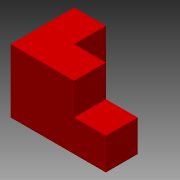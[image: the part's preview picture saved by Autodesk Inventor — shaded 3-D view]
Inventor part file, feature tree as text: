
AUTODESK INVENTOR PART (.ipt)
format: ipt  version: 2013 (Build 170138000, 138)  size: 99,840 bytes
history: native  units: in
note: dims shown in document units (in); Inventor stores cm internally (conversion verified against a paired STEP export)
features: extrude x3, sketch x3
ambient origin geometry x8: Origin, YZ Plane, XZ Plane, XY Plane, X Axis, Y Axis, Z Axis, Center Point
bodies: Solid1 (feature_tree)
feature tree (6):
  extrude  "Extrusion1"  Depth=0.75in
  extrude  "Extrusion2"  Depth=1.5in
  extrude  "Extrusion3"  Depth=0.75in TaperAngle=0.0deg
  sketch  "Sketch1"  dims[d0=2.25in d1=0.75in]
  sketch  "Sketch2"  dims[d2=0.75in d3=0.0in d4=1.5in]
  sketch  "Sketch3"  dims[d5=0.75in d6=0.75in d7=0.0in d8=0.75in d9=0.75in d10=0.75in d11=0.0in]
